# Revit family: Deca_Sifão para lavatório_Sifoes Luxo_1684.100.112
name_source: partatom
category: Plumbing Fixtures
units: mm (PartAtom-declared; Revit-internal decimal feet)

## family parameters
Cut with Voids When Loaded = No
Host = Face
Part Type = Normal
Room Calculation Point = No
Round Connector Dimension = Use Radius
Shared = No

## types (5) — shared parameters
Acompanha o Produto = -
Aprovado por = quattroD
Atendimento ao Cliente = 0800-0117073
Categoria = COMPLEMENTARES
Composição Anel Vedação = -
Composição Assento = -
Composição Básica = Liga de Cobre (bronze e latão),Plásticos de Engenharia,Elastômeros
Composição Componente = -
Consumo = -
Cor Interna = -
Cor Secundária = -
Cores Componente = -
Criado por = quattroD
Código Pai = 1684.100.112
Default Elevation = 500 mm
Description = Sifão para lavatório
Diâmetro Entrada de Esgoto = 25 mm  [stored 0.082021 ft]
Diâmetro Ponto de Esgoto = 40 mm
Informações Complementares = -
Itens de Instalação = -
Linha = Sifoes Luxo
Manufacturer = Deca
Norma = NBR14162
Peso Líquido (Kg) = 1.264
Pressão máx. funcionamento = -
Pressão mín. Aquec. Acúmulo = -
Pressão mín. Aquec. Passagem = -
Pressão mín. funcionamento = -
Raio Entrada de Esgoto = 13 mm
Raio Ponto de Esgoto = 20 mm  [stored 0.0656168 ft]
Saída de Esgoto = -
Segmento = Banheiro Luxo
Tipo de dispositivo economizador = -
Tipo de mecanismo utilizado = -
Tipo de rosca de entrada = BSP NBR 8133
Tipo de rosca de saída = -
URL = www.deca.com.br
Vazão na Pressão máx. (L/min) = -
Vazão na Pressão mín. (L/min) = -
zero-valued in all types: CWFU, WFU

## per-type parameters (varying)
| type | Cor Principal | Distância Auxiliar | Distância Auxiliar Interna | Material | Model |
| 1684.C.100.112_Cromado | Cromado | 200 mm | 180 mm | Deca_Cromado | 1684.C.100.112 |
| 1684.BL.100.112.MT_Black Matte | Black Matte | 0 mm  [stored 0 ft] | 110 mm  [stored 0.360892 ft] | Deca_Black Matte | 1684.BL.100.112.MT |
| 1684.CT.100.112.MT_Corten | Corten | 0 mm  [stored 0 ft] | 110 mm  [stored 0.360892 ft] | Deca_Corten | 1684.CT.100.112.MT |
| 1684.GL.100.112.MT_Gold Matte | Gold Matte | 0 mm  [stored 0 ft] | 110 mm  [stored 0.360892 ft] | Deca_Gold Matte | 1684.GL.100.112.MT |
| 1684.GL.100.112.RD_Red Gold | Red Gold | 0 mm  [stored 0 ft] | 110 mm  [stored 0.360892 ft] | Deca_Red Gold | 1684.GL.100.112.RD |

note: [stored X ft] marks values corroborated as IEEE doubles in the binary element streams (Revit-internal decimal feet)

## geometry (parser evidence)
native form markers: Sweep x1
no freeform markers — native parametric forms only
